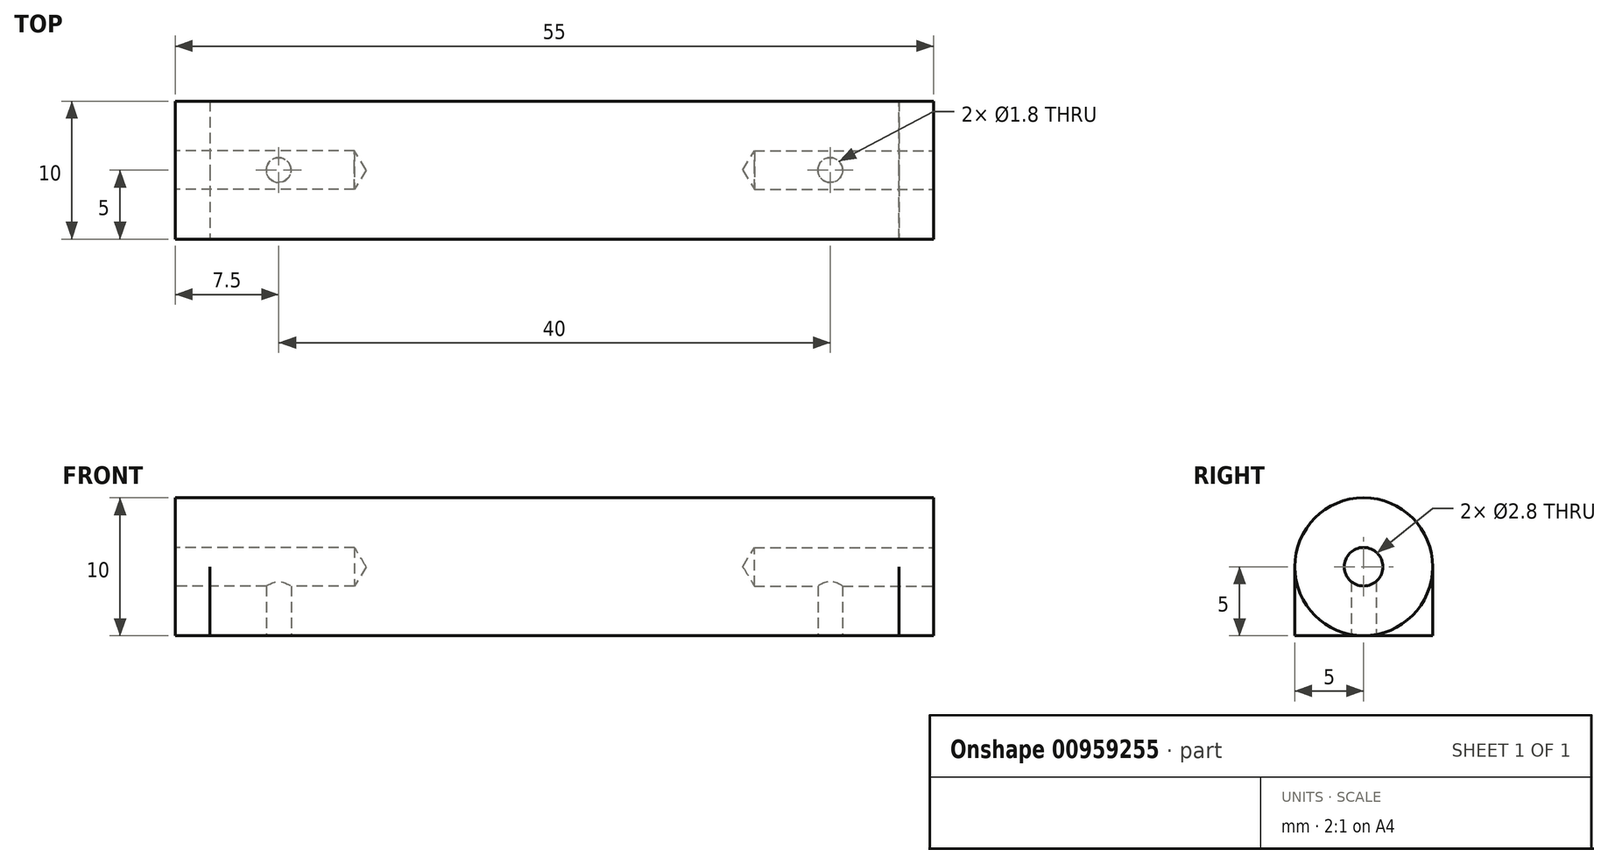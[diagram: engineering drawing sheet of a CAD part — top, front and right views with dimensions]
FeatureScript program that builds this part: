
annotation { "Feature Type Name" : "Feature", "Feature Type Description" : "" }
export const myFeature = defineFeature(function(context is Context, id is Id, definition is map)
    precondition{}
    {
        {
            var Q0;
            Q0=qCreatedBy(makeId("Top.planeOp"),FACE);
            var sketch = newSketch(context, id + "F0", { "sketchPlane" : qUnion([Q0])});
            skLineSegment(sketch, "E0.bottom", {"start": v(-27.5, 5) * mm, "end": v(27.5, 5) * mm});
            skLineSegment(sketch, "E0.top", {"start": v(-27.5, -5) * mm, "end": v(27.5, -5) * mm});
            skLineSegment(sketch, "E0.left", {"start": v(-27.5, 5) * mm, "end": v(-27.5, -5) * mm});
            skLineSegment(sketch, "E0.right", {"start": v(27.5, 5) * mm, "end": v(27.5, -5) * mm});
            skPoint(sketch, "E0.middle", {"position": v(0, 0) * mm});
            skSolve(sketch);
        }
        {
            var Q0;
            Q0 = qSketchRegion(id + "F0", true);
            extrude(context, id + "F1", {"entities" : qUnion([Q0]), "depth" : 10 * mm, "offsetDistance" : 25 * mm});
        }
        {
            var Q0;
            Q0=makeQuery(id+"F1.opExtrude","SWEPT_FACE",FACE,{"disambiguationData":[OSD([sQuery(id+"F0.wireOp",EDGE,"E0.left")])]});
            var sketch = newSketch(context, id + "F2", { "sketchPlane" : qUnion([Q0])});
            skPoint(sketch, "E1", {"position": v(0, 5) * mm});
            skPoint(sketch, "E1.positionSnap0", {"position": v(0, 10) * mm});
            skSolve(sketch);
        }
        {
            var Q0;
            Q0=sQuery(id+"F2.wireOp",VERTEX,"E1");
            var Q1;
            Q1=makeQuery(id+"F1.opExtrude","SWEPT_BODY",BODY,{"disambiguationData":[OSD([sQuery(id+"F0.wireOp",EDGE,"E0.bottom"),sQuery(id+"F0.wireOp",EDGE,"E0.top"),sQuery(id+"F0.wireOp",EDGE,"E0.left"),sQuery(id+"F0.wireOp",EDGE,"E0.right")])]});
            hole(context, id + "F3", {"style" : HoleStyle.SIMPLE, "endStyle" : HoleEndStyle.BLIND, "holeDiameter" : 2.8 * mm, "majorDiameter" : 5 * mm, "holeDepth" : 13 * mm, "isTappedThrough" : true, "tappedDepth" : 12 * mm, "tapClearance" : 3, "locations" : qUnion([Q0]), "scope" : qUnion([Q1])});
        }
        {
            var Q0;
            Q0=makeQuery(id+"F1.opExtrude","SWEPT_FACE",FACE,{"disambiguationData":[OSD([sQuery(id+"F0.wireOp",EDGE,"E0.right")])]});
            var sketch = newSketch(context, id + "F4", { "sketchPlane" : qUnion([Q0])});
            skPoint(sketch, "E2", {"position": v(0, 5) * mm});
            skSolve(sketch);
        }
        {
            var Q0;
            Q0=sQuery(id+"F4.wireOp",VERTEX,"E2");
            var Q1;
            Q1=makeQuery(id+"F1.opExtrude","SWEPT_BODY",BODY,{"disambiguationData":[OSD([sQuery(id+"F0.wireOp",EDGE,"E0.bottom"),sQuery(id+"F0.wireOp",EDGE,"E0.top"),sQuery(id+"F0.wireOp",EDGE,"E0.left"),sQuery(id+"F0.wireOp",EDGE,"E0.right")])]});
            hole(context, id + "F5", {"style" : HoleStyle.SIMPLE, "endStyle" : HoleEndStyle.BLIND, "holeDiameter" : 2.8 * mm, "majorDiameter" : 5 * mm, "holeDepth" : 13 * mm, "isTappedThrough" : true, "tappedDepth" : 12 * mm, "tapClearance" : 3, "locations" : qUnion([Q0]), "scope" : qUnion([Q1])});
        }
        {
            var Q0;
            Q0=makeQuery(id+"F1.opExtrude","SWEPT_FACE",FACE,{"disambiguationData":[OSD([sQuery(id+"F0.wireOp",EDGE,"E0.right")])]});
            var sketch = newSketch(context, id + "F6", { "sketchPlane" : qUnion([Q0])});
            skCircle(sketch, "E3", {"center": v(0, 5) * mm, "radius": 5 * mm});
            skSolve(sketch);
        }
        {
            var Q0;
            {var subQ0=sQuery(id+"F6.wireOp",EDGE,"E3");var subQ1=sQuery(id+"F0.wireOp",EDGE,"E0.right");var subQ4=makeQuery(id+"F1.opExtrude","CAP_EDGE",EDGE,{"disambiguationData":[OSD([subQ1])],"isStart":true});var subQ5=makeQuery(id+"F6.imprint","INTERSECT",VERTEX,{"derivedFrom":[subQ4,subQ0]});Q0=makeQuery(id+"F6.imprint","IMPRINT",FACE,{"disambiguationData":[TD([[makeQuery(id+"F6.imprint","IMPRINT",EDGE,{"disambiguationData":[TD([[subQ5,-1.0]])],"derivedFrom":subQ0}),-1.0]])]});}
            var Q1;
            {var subQ0=sQuery(id+"F6.wireOp",EDGE,"E3");var subQ1=sQuery(id+"F0.wireOp",EDGE,"E0.right");var subQ4=makeQuery(id+"F1.opExtrude","CAP_EDGE",EDGE,{"disambiguationData":[OSD([subQ1])],"isStart":true});var subQ5=makeQuery(id+"F6.imprint","INTERSECT",VERTEX,{"derivedFrom":[subQ4,subQ0]});Q1=makeQuery(id+"F6.imprint","IMPRINT",FACE,{"disambiguationData":[TD([[makeQuery(id+"F6.imprint","IMPRINT",EDGE,{"disambiguationData":[TD([[subQ5,1.0]])],"derivedFrom":subQ0}),-1.0]])]});}
            extrude(context, id + "F7", {"entities" : qUnion([Q0, Q1]), "operationType" : NewBodyOperationType.REMOVE, "oppositeDirection" : true, "depth" : 2.5 * mm, "offsetDistance" : 25 * mm});
        }
        {
            var Q0;
            Q0=makeQuery(id+"F1.opExtrude","SWEPT_FACE",FACE,{"disambiguationData":[OSD([sQuery(id+"F0.wireOp",EDGE,"E0.left")])]});
            var sketch = newSketch(context, id + "F8", { "sketchPlane" : qUnion([Q0])});
            skCircle(sketch, "E4", {"center": v(0, 5) * mm, "radius": 5 * mm});
            skSolve(sketch);
        }
        {
            var Q0;
            {var subQ0=sQuery(id+"F8.wireOp",EDGE,"E4");var subQ1=sQuery(id+"F0.wireOp",EDGE,"E0.left");var subQ4=makeQuery(id+"F1.opExtrude","CAP_EDGE",EDGE,{"disambiguationData":[OSD([subQ1])],"isStart":true});var subQ5=makeQuery(id+"F8.imprint","INTERSECT",VERTEX,{"derivedFrom":[subQ4,subQ0]});Q0=makeQuery(id+"F8.imprint","IMPRINT",FACE,{"disambiguationData":[TD([[makeQuery(id+"F8.imprint","IMPRINT",EDGE,{"disambiguationData":[TD([[subQ5,1.0]])],"derivedFrom":subQ0}),-1.0]])]});}
            var Q1;
            {var subQ0=sQuery(id+"F8.wireOp",EDGE,"E4");var subQ1=sQuery(id+"F0.wireOp",EDGE,"E0.left");var subQ4=makeQuery(id+"F1.opExtrude","CAP_EDGE",EDGE,{"disambiguationData":[OSD([subQ1])],"isStart":true});var subQ5=makeQuery(id+"F8.imprint","INTERSECT",VERTEX,{"derivedFrom":[subQ4,subQ0]});Q1=makeQuery(id+"F8.imprint","IMPRINT",FACE,{"disambiguationData":[TD([[makeQuery(id+"F8.imprint","IMPRINT",EDGE,{"disambiguationData":[TD([[subQ5,-1.0]])],"derivedFrom":subQ0}),-1.0]])]});}
            var Q2;
            Q2=makeQuery(id+"F8.imprint","IMPRINT",FACE,{"disambiguationData":[TD([[makeQuery(id+"F8.imprint","IMPRINT",EDGE,{"derivedFrom":makeQuery(id+"F3.hole-0.boolean.opBoolean","COPY",EDGE,{"derivedFrom":makeQuery(id+"F3.hole-0.opRevolve","SWEPT_EDGE",EDGE,{"disambiguationData":[OSD([sQuery(id+"F3.hole-0.sketch.wireOp",EDGE,"core_line_2"),sQuery(id+"F3.hole-0.sketch.wireOp",EDGE,"core_line_3")])]})})}),1.0]])]});
            extrude(context, id + "F9", {"entities" : qUnion([Q0, Q1, Q2]), "operationType" : NewBodyOperationType.REMOVE, "oppositeDirection" : true, "depth" : 2.5 * mm, "offsetDistance" : 25 * mm});
        }
        {
            var Q0;
            Q0=makeQuery(id+"F1.opExtrude","CAP_EDGE",EDGE,{"disambiguationData":[OSD([sQuery(id+"F0.wireOp",EDGE,"E0.bottom")])],"isStart":false});
            var Q1;
            Q1=makeQuery(id+"F1.opExtrude","CAP_EDGE",EDGE,{"disambiguationData":[OSD([sQuery(id+"F0.wireOp",EDGE,"E0.top")])],"isStart":false});
            fillet(context, id + "F10", {"entities" : qUnion([Q0, Q1]), "radius" : 5 * mm, "tangentPropagation" : true, "allowEdgeOverflow" : false});
        }
        {
            var Q0;
            Q0=makeQuery(id+"F1.opExtrude","CAP_FACE",FACE,{"disambiguationData":[OSD([sQuery(id+"F0.wireOp",EDGE,"E0.bottom"),sQuery(id+"F0.wireOp",EDGE,"E0.top"),sQuery(id+"F0.wireOp",EDGE,"E0.left"),sQuery(id+"F0.wireOp",EDGE,"E0.right")])],"isStart":true});
            var sketch = newSketch(context, id + "F11", { "sketchPlane" : qUnion([Q0])});
            skLineSegment(sketch, "E5.bottom", {"start": v(-20, 2.5) * mm, "end": v(20, 2.5) * mm});
            skLineSegment(sketch, "E5.top", {"start": v(-20, -2.5) * mm, "end": v(20, -2.5) * mm});
            skLineSegment(sketch, "E5.left", {"start": v(-20, 2.5) * mm, "end": v(-20, -2.5) * mm});
            skLineSegment(sketch, "E5.right", {"start": v(20, 2.5) * mm, "end": v(20, -2.5) * mm});
            skPoint(sketch, "E6", {"position": v(-20, 0) * mm});
            skPoint(sketch, "E7", {"position": v(20, 0) * mm});
            skSolve(sketch);
        }
        {
            var Q0;
            Q0=sQuery(id+"F11.wireOp",VERTEX,"E6");
            var Q1;
            Q1=sQuery(id+"F11.wireOp",VERTEX,"E5.middle");
            var Q2;
            Q2=sQuery(id+"F11.wireOp",VERTEX,"E7");
            var Q3;
            Q3=makeQuery(id+"F1.opExtrude","SWEPT_BODY",BODY,{"disambiguationData":[OSD([sQuery(id+"F0.wireOp",EDGE,"E0.bottom"),sQuery(id+"F0.wireOp",EDGE,"E0.top"),sQuery(id+"F0.wireOp",EDGE,"E0.left"),sQuery(id+"F0.wireOp",EDGE,"E0.right")])]});
            hole(context, id + "F12", {"style" : HoleStyle.SIMPLE, "endStyle" : HoleEndStyle.BLIND, "holeDiameter" : 1.8 * mm, "majorDiameter" : 5 * mm, "holeDepth" : 5 * mm, "isTappedThrough" : true, "tappedDepth" : 12 * mm, "tapClearance" : 3, "locations" : qUnion([Q0, Q1, Q2]), "scope" : qUnion([Q3])});
        }
    });
